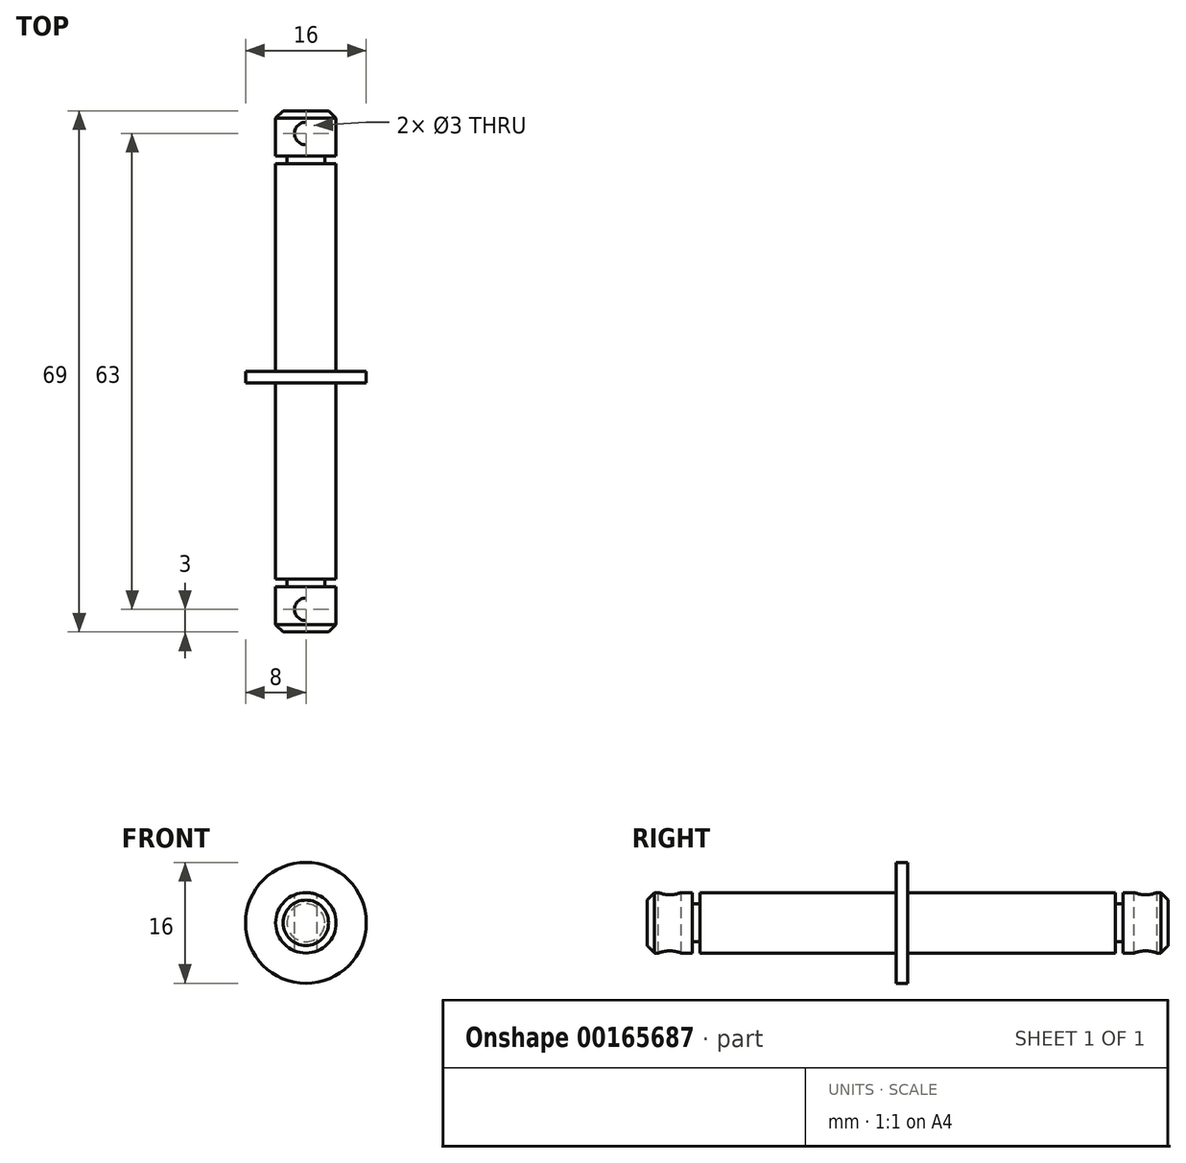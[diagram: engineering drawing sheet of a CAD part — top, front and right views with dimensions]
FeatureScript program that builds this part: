
annotation { "Feature Type Name" : "Feature", "Feature Type Description" : "" }
export const myFeature = defineFeature(function(context is Context, id is Id, definition is map)
    precondition{}
    {
        {
            var Q0;
            Q0=qCreatedBy(makeId("Front.planeOp"),FACE);
            var sketch = newSketch(context, id + "F0", { "sketchPlane" : qUnion([Q0])});
            skCircle(sketch, "E0", {"center": v(0, 0) * mm, "radius": 4 * mm});
            skCircle(sketch, "E1", {"center": v(0, 0) * mm, "radius": 8 * mm});
            skSolve(sketch);
        }
        {
            var Q0;
            Q0=makeQuery(id+"F0.imprint","IMPRINT",FACE,{"disambiguationData":[TD([[makeQuery(id+"F0.imprint","IMPRINT",EDGE,{"derivedFrom":sQuery(id+"F0.wireOp",EDGE,"E0")}),-1.0]])]});
            extrude(context, id + "F1", {"entities" : qUnion([Q0]), "depth" : 1.5 * mm, "offsetDistance" : 25 * mm});
        }
        {
            var Q0;
            Q0=qCreatedBy(makeId("Front.planeOp"),FACE);
            var sketch = newSketch(context, id + "F2", { "sketchPlane" : qUnion([Q0]) });
            skCircle(sketch, "E2", {"center": v(0, 0) * mm, "radius": 4 * mm});
            skSolve(sketch);
        }
        {
            var Q0;
            Q0=makeQuery(id+"F2.imprint","IMPRINT",FACE,{"disambiguationData":[TD([[makeQuery(id+"F2.imprint","IMPRINT",EDGE,{"derivedFrom":sQuery(id+"F2.wireOp",EDGE,"E2")}),1.0]])]});
            var Q1;
            Q1=sQuery(id+"F2.wireOp",EDGE,"E2");
            extrude(context, id + "F3", {"entities" : qUnion([Q0]), "surfaceEntities" : qUnion([Q1]), "depth" : 34.5 * mm, "offsetDistance" : 25 * mm});
        }
        {
            var Q0;
            Q0=makeQuery(id+"F3.opExtrude","CAP_FACE",FACE,{"disambiguationData":[OSD([sQuery(id+"F2.wireOp",EDGE,"E2")])],"isStart":false});
            cPlane(context, id + "F4", {"entities" : qUnion([Q0]), "cplaneType" : CPlaneType.OFFSET, "offset" : 6 * mm, "oppositeDirection" : true, "width" : 150 * mm, "height" : 150 * mm});
        }
        {
            var Q0;
            Q0=qCreatedBy(id+"F4.planeOp",FACE);
            var sketch = newSketch(context, id + "F5", { "sketchPlane" : qUnion([Q0]) });
            skCircle(sketch, "E3", {"center": v(0, 0) * mm, "radius": 2.5 * mm});
            skCircle(sketch, "E4.0", {"center": v(0, 0) * mm, "radius": 4 * mm});
            skSolve(sketch);
        }
        {
            var Q0;
            Q0 = qSketchRegion(id + "F5", true);
            extrude(context, id + "F6", {"entities" : qUnion([Q0]), "operationType" : NewBodyOperationType.REMOVE, "oppositeDirection" : true, "depth" : 1 * mm, "offsetDistance" : 25 * mm});
        }
        {
            var Q0;
            Q0=makeQuery(id+"F3.opExtrude","CAP_EDGE",EDGE,{"disambiguationData":[OSD([sQuery(id+"F2.wireOp",EDGE,"E2")])],"isStart":false});
            chamfer(context, id + "F7", {"entities" : qUnion([Q0]), "width" : 1 * mm, "tangentPropagation" : true});
        }
        {
            var Q0;
            Q0=qCreatedBy(makeId("Top.planeOp"),FACE);
            var sketch = newSketch(context, id + "F8", { "sketchPlane" : qUnion([Q0]) });
            skCircle(sketch, "E5", {"center": v(0, -31.5) * mm, "radius": 1.5 * mm});
            skSolve(sketch);
        }
        {
            var Q0;
            Q0 = qSketchRegion(id + "F8", true);
            extrude(context, id + "F9", {"entities" : qUnion([Q0]), "operationType" : NewBodyOperationType.REMOVE, "endBound" : BoundingType.SYMMETRIC, "oppositeDirection" : true, "depth" : 8 * mm, "offsetDistance" : 25 * mm});
        }
        {
            var Q0;
            Q0=makeQuery(id+"F3.opExtrude","SWEPT_BODY",BODY,{"disambiguationData":[OSD([sQuery(id+"F2.wireOp",EDGE,"E2")])]});
            var Q1;
            Q1=qCreatedBy(makeId("Front.planeOp"),FACE);
            mirror(context, id + "F10", {"operationType" : NewBodyOperationType.ADD, "entities" : qUnion([Q0]), "mirrorPlane" : qUnion([Q1])});
        }
    });
